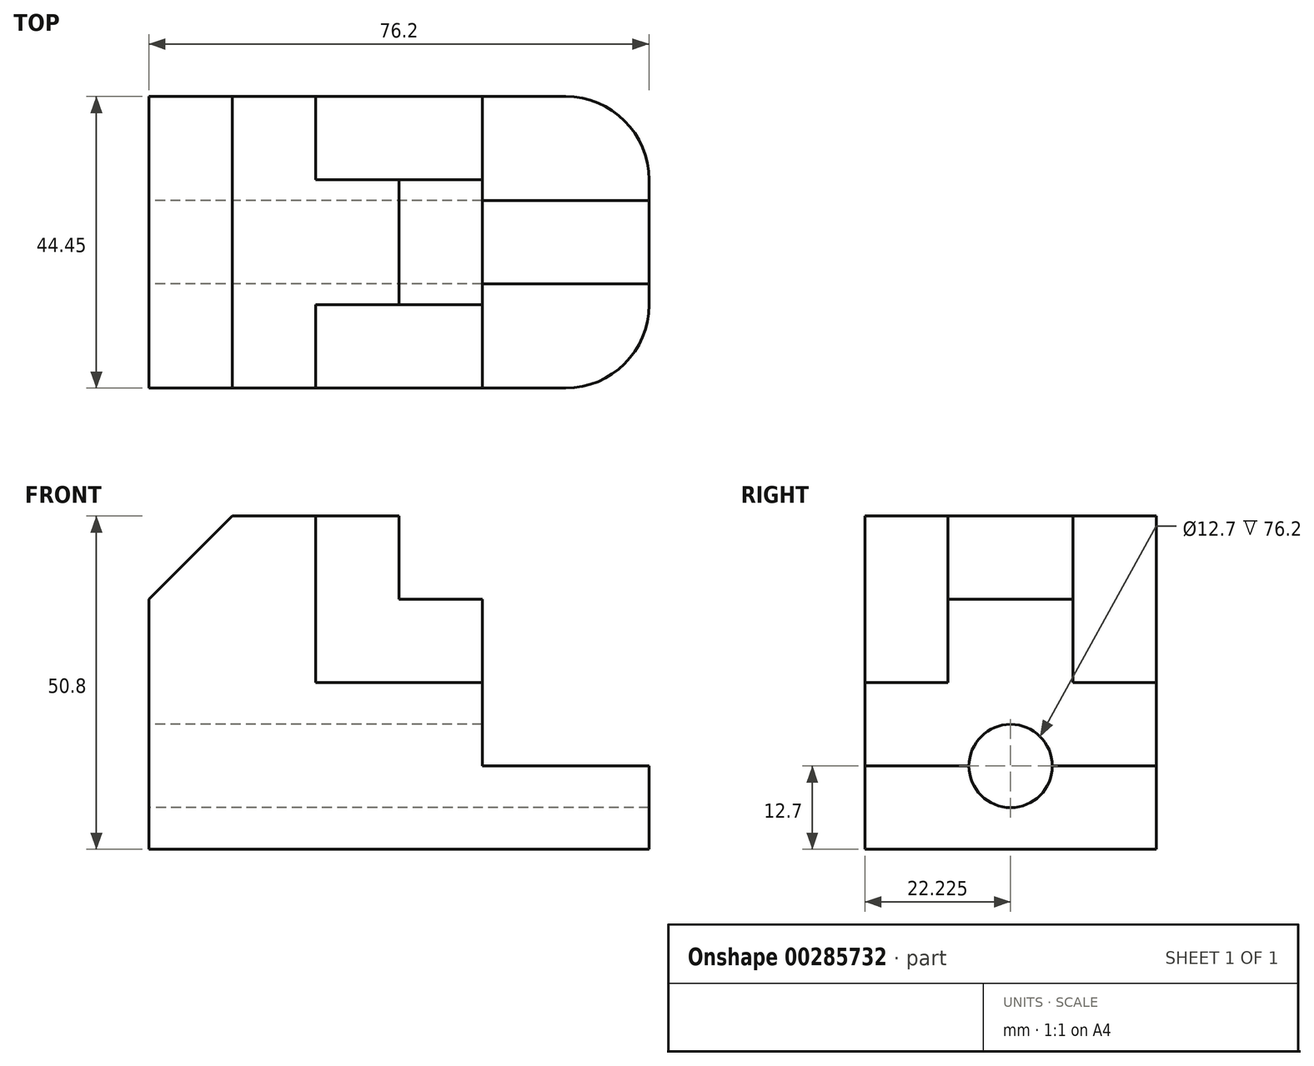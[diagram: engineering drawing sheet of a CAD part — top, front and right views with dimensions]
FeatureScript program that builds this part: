
annotation { "Feature Type Name" : "Feature", "Feature Type Description" : "" }
export const myFeature = defineFeature(function(context is Context, id is Id, definition is map)
    precondition{}
    {
        {
            var Q0;
            Q0=qCreatedBy(makeId("Top.planeOp"),FACE);
            var sketch = newSketch(context, id + "F0", { "sketchPlane" : qUnion([Q0])});
            skLineSegment(sketch, "E0", {"start": v(0, 0) * mm, "end": v(0, 44.45) * mm});
            skLineSegment(sketch, "E1", {"start": v(0, 44.45) * mm, "end": v(63.5, 44.45) * mm});
            skLineSegment(sketch, "E2", {"start": v(0, 0) * mm, "end": v(63.5, 0) * mm});
            skLineSegment(sketch, "E3", {"start": v(76.2, 31.75) * mm, "end": v(76.2, 12.7) * mm});
            skArc(sketch, "E4", {"start": v(76.2, 31.75) * mm, "mid": v(72.48, 40.73) * mm, "end": v(63.5, 44.45) * mm});
            skArc(sketch, "E5", {"start": v(63.5, 0) * mm, "mid": v(72.48, 3.72) * mm, "end": v(76.2, 12.7) * mm});
            skSolve(sketch);
        }
        {
            var Q0;
            Q0 = qSketchRegion(id + "F0", true);
            extrude(context, id + "F1", {"entities" : qUnion([Q0]), "depth" : 50.8 * mm});
        }
        {
            var Q0;
            Q0=makeQuery(id+"F1.opExtrude","CAP_FACE",FACE,{"disambiguationData":[OSD([sQuery(id+"F0.wireOp",EDGE,"E0"),sQuery(id+"F0.wireOp",EDGE,"E1"),sQuery(id+"F0.wireOp",EDGE,"E2"),sQuery(id+"F0.wireOp",EDGE,"E3"),sQuery(id+"F0.wireOp",EDGE,"E4"),sQuery(id+"F0.wireOp",EDGE,"E5")])],"isStart":false});
            var sketch = newSketch(context, id + "F2", { "sketchPlane" : qUnion([Q0])});
            skLineSegment(sketch, "E6.bottom", {"start": v(25.4, 44.45) * mm, "end": v(50.8, 44.45) * mm});
            skLineSegment(sketch, "E6.top", {"start": v(25.4, 31.75) * mm, "end": v(50.8, 31.75) * mm});
            skLineSegment(sketch, "E6.left", {"start": v(25.4, 44.45) * mm, "end": v(25.4, 31.75) * mm});
            skLineSegment(sketch, "E6.right", {"start": v(50.8, 44.45) * mm, "end": v(50.8, 31.75) * mm});
            skLineSegment(sketch, "E7.bottom", {"start": v(25.4, 0) * mm, "end": v(50.8, 0) * mm});
            skLineSegment(sketch, "E7.top", {"start": v(25.4, 12.7) * mm, "end": v(50.8, 12.7) * mm});
            skLineSegment(sketch, "E7.left", {"start": v(25.4, 0) * mm, "end": v(25.4, 12.7) * mm});
            skLineSegment(sketch, "E7.right", {"start": v(50.8, 0) * mm, "end": v(50.8, 12.7) * mm});
            skLineSegment(sketch, "E8", {"start": v(50.8, 44.45) * mm, "end": v(50.8, 0) * mm});
            skLineSegment(sketch, "E9", {"start": v(38.1, 31.75) * mm, "end": v(38.1, 12.7) * mm});
            skSolve(sketch);
        }
        {
            var Q0;
            {var subQ5=sQuery(id+"F2.wireOp",EDGE,"E6.bottom");Q0=makeQuery(id+"F2.imprint","IMPRINT",FACE,{"disambiguationData":[TD([[makeQuery(id+"F2.imprint","IMPRINT",EDGE,{"derivedFrom":subQ5}),-1.0]])]});}
            var Q1;
            {var subQ5=sQuery(id+"F2.wireOp",EDGE,"E7.bottom");Q1=makeQuery(id+"F2.imprint","IMPRINT",FACE,{"disambiguationData":[TD([[makeQuery(id+"F2.imprint","IMPRINT",EDGE,{"derivedFrom":subQ5}),1.0]])]});}
            extrude(context, id + "F3", {"entities" : qUnion([Q0, Q1]), "operationType" : NewBodyOperationType.REMOVE, "oppositeDirection" : true, "depth" : 25.4 * mm});
        }
        {
            var Q0;
            Q0=makeQuery(id+"F2.imprint","IMPRINT",FACE,{"disambiguationData":[TD([[makeQuery(id+"F2.imprint","IMPRINT",EDGE,{"derivedFrom":makeQuery(id+"F1.opExtrude","CAP_EDGE",EDGE,{"disambiguationData":[OSD([sQuery(id+"F0.wireOp",EDGE,"E3")])],"isStart":false})}),-1.0]])]});
            extrude(context, id + "F4", {"entities" : qUnion([Q0]), "operationType" : NewBodyOperationType.REMOVE, "oppositeDirection" : true, "depth" : 38.1 * mm});
        }
        {
            var Q0;
            {var subQ3=sQuery(id+"F2.wireOp",EDGE,"E9");Q0=makeQuery(id+"F2.imprint","IMPRINT",FACE,{"disambiguationData":[TD([[makeQuery(id+"F2.imprint","IMPRINT",EDGE,{"derivedFrom":subQ3}),1.0]])]});}
            extrude(context, id + "F5", {"entities" : qUnion([Q0]), "operationType" : NewBodyOperationType.REMOVE, "oppositeDirection" : true, "depth" : 12.7 * mm});
        }
        {
            var Q0;
            Q0=makeQuery(id+"F1.opExtrude","SWEPT_FACE",FACE,{"disambiguationData":[OSD([sQuery(id+"F0.wireOp",EDGE,"E2")])]});
            var sketch = newSketch(context, id + "F6", { "sketchPlane" : qUnion([Q0])});
            skLineSegment(sketch, "E10", {"start": v(0, 38.1) * mm, "end": v(12.7, 50.8) * mm});
            skSolve(sketch);
        }
        {
            var Q0;
            {var subQ0=sQuery(id+"F6.wireOp",EDGE,"E10");Q0=makeQuery(id+"F6.imprint","IMPRINT",FACE,{"disambiguationData":[TD([[makeQuery(id+"F6.imprint","IMPRINT",EDGE,{"derivedFrom":subQ0}),1.0]])]});}
            var Q1;
            Q1=makeQuery(id+"F1.opExtrude","SWEPT_FACE",FACE,{"disambiguationData":[OSD([sQuery(id+"F0.wireOp",EDGE,"E1")])]});
            extrude(context, id + "F7", {"entities" : qUnion([Q0]), "operationType" : NewBodyOperationType.REMOVE, "endBound" : BoundingType.UP_TO_SURFACE, "oppositeDirection" : true, "endBoundEntityFace" : qUnion([Q1]), "depth" : 25.4 * mm});
        }
        {
            var Q0;
            Q0=makeQuery(id+"F1.opExtrude","SWEPT_FACE",FACE,{"disambiguationData":[OSD([sQuery(id+"F0.wireOp",EDGE,"E0")])]});
            var sketch = newSketch(context, id + "F8", { "sketchPlane" : qUnion([Q0])});
            skCircle(sketch, "E11", {"center": v(-22.23, 12.7) * mm, "radius": 6.35 * mm});
            skSolve(sketch);
        }
        {
            var Q0;
            Q0 = qSketchRegion(id + "F8", true);
            var Q1;
            Q1=makeQuery(id+"F1.opExtrude","SWEPT_FACE",FACE,{"disambiguationData":[OSD([sQuery(id+"F0.wireOp",EDGE,"E3")])]});
            extrude(context, id + "F9", {"entities" : qUnion([Q0]), "operationType" : NewBodyOperationType.REMOVE, "endBound" : BoundingType.UP_TO_SURFACE, "oppositeDirection" : true, "endBoundEntityFace" : qUnion([Q1]), "depth" : 25.4 * mm});
        }
    });
